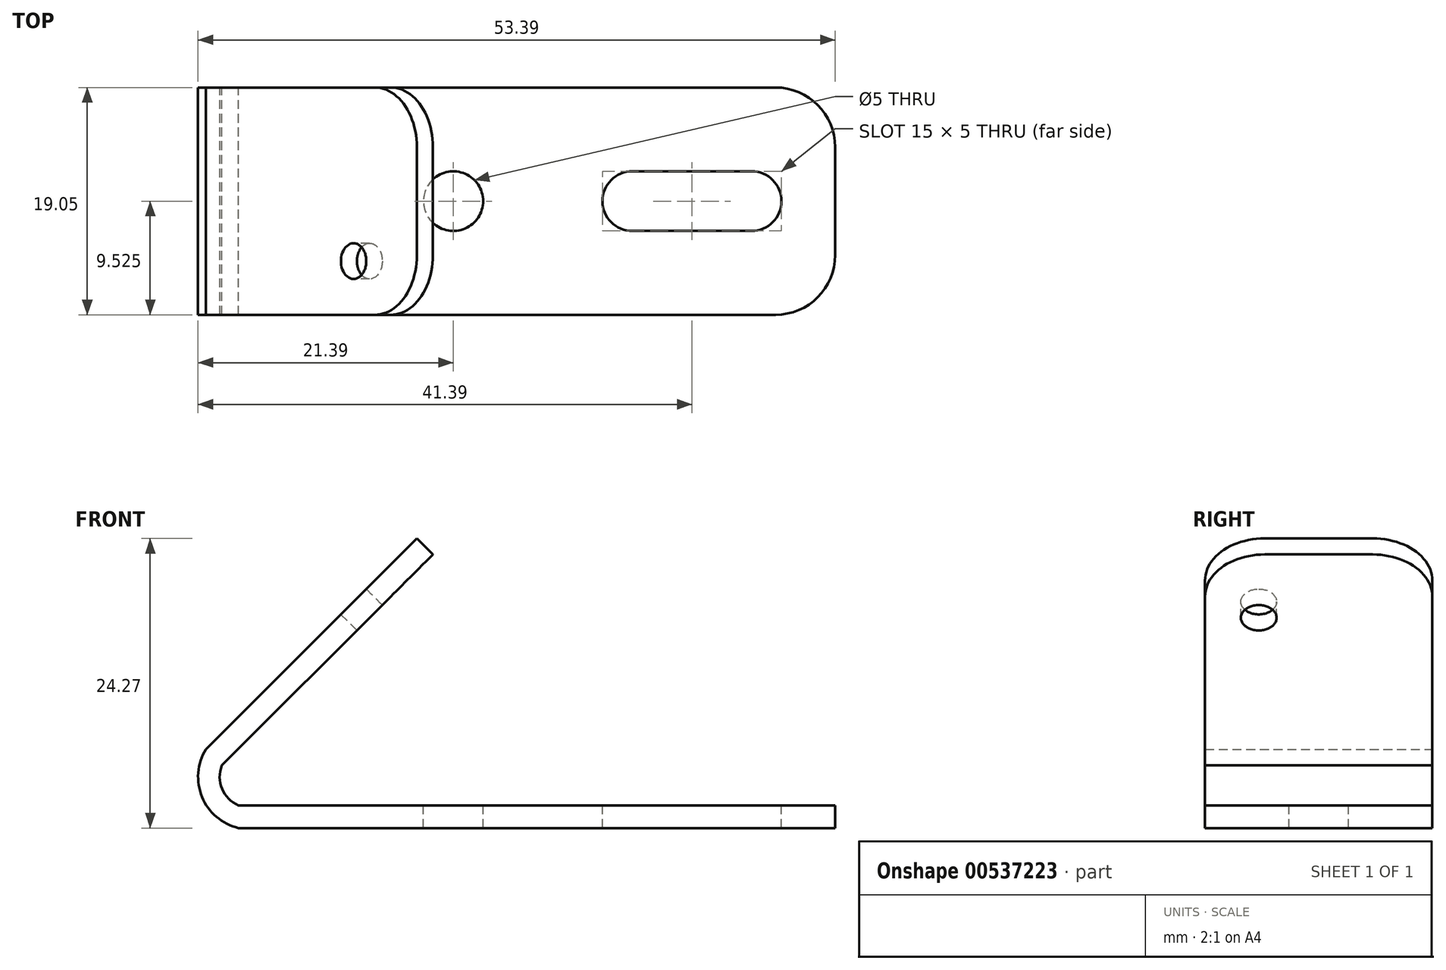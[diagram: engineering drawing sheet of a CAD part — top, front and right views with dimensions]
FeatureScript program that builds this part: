
annotation { "Feature Type Name" : "Feature", "Feature Type Description" : "" }
export const myFeature = defineFeature(function(context is Context, id is Id, definition is map)
    precondition{}
    {
        {
            var Q0;
            Q0=qCreatedBy(makeId("Front.planeOp"),FACE);
            var sketch = newSketch(context, id + "F0", { "sketchPlane" : qUnion([Q0])});
            skLineSegment(sketch, "E0", {"start": v(0, 0) * mm, "end": v(50, 0) * mm});
            skLineSegment(sketch, "E1", {"start": v(50, 0) * mm, "end": v(50, 1.9) * mm});
            skLineSegment(sketch, "E2", {"start": v(50, 1.9) * mm, "end": v(0, 1.9) * mm});
            skLineSegment(sketch, "E3", {"start": v(-2.73, 6.6) * mm, "end": v(14.95, 24.27) * mm});
            skArc(sketch, "E4", {"start": v(-2.73, 6.6) * mm, "mid": v(-3.05, 2.6) * mm, "end": v(0, 0) * mm});
            skLineSegment(sketch, "E5", {"start": v(14.95, 24.27) * mm, "end": v(16.29, 22.93) * mm});
            skLineSegment(sketch, "E6", {"start": v(16.29, 22.93) * mm, "end": v(-1.39, 5.25) * mm});
            skArc(sketch, "E7", {"start": v(0, 1.9) * mm, "mid": v(-1.38, 3.3) * mm, "end": v(-1.39, 5.25) * mm});
            skSolve(sketch);
        }
        {
            var Q0;
            Q0 = qSketchRegion(id + "F0", true);
            extrude(context, id + "F1", {"entities" : qUnion([Q0]), "depth" : 19.05 * mm, "offsetDistance" : 25 * mm});
        }
        {
            var Q0;
            Q0=makeQuery(id+"F1.opExtrude","CAP_EDGE",EDGE,{"disambiguationData":[OSD([sQuery(id+"F0.wireOp",EDGE,"E5")])],"isStart":false});
            var Q1;
            Q1=makeQuery(id+"F1.opExtrude","CAP_EDGE",EDGE,{"disambiguationData":[OSD([sQuery(id+"F0.wireOp",EDGE,"E5")])],"isStart":true});
            fillet(context, id + "F2", {"entities" : qUnion([Q0, Q1]), "radius" : 5 * mm, "tangentPropagation" : true, "allowEdgeOverflow" : false});
        }
        {
            var Q0;
            Q0=makeQuery(id+"F1.opExtrude","SWEPT_FACE",FACE,{"disambiguationData":[OSD([sQuery(id+"F0.wireOp",EDGE,"E3")])]});
            var sketch = newSketch(context, id + "F3", { "sketchPlane" : qUnion([Q0])});
            skLineSegment(sketch, "E8", {"start": v(19.05, 27.73) * mm, "end": v(14.55, 27.73) * mm, "construction": true});
            skLineSegment(sketch, "E9", {"start": v(14.55, 27.73) * mm, "end": v(14.55, 20.23) * mm, "construction": true});
            skCircle(sketch, "E10", {"center": v(14.55, 20.23) * mm, "radius": 1.5 * mm});
            skLineSegment(sketch, "E11", {"start": v(9.53, 42.7) * mm, "end": v(9.53, -11.02) * mm, "construction": true});
            skPoint(sketch, "E11.startSnap0", {"position": v(9.53, 27.73) * mm});
            skCircle(sketch, "E12.MirrorC", {"center": v(4.5, 20.23) * mm, "radius": 1.5 * mm});
            skSolve(sketch);
        }
        {
            var Q0;
            Q0=makeQuery(id+"F3.imprint","IMPRINT",FACE,{"disambiguationData":[TD([[makeQuery(id+"F3.imprint","IMPRINT",EDGE,{"derivedFrom":sQuery(id+"F3.wireOp",EDGE,"E10")}),1.0]])]});
            extrude(context, id + "F4", {"entities" : qUnion([Q0]), "operationType" : NewBodyOperationType.REMOVE, "oppositeDirection" : true, "depth" : 10 * mm, "offsetDistance" : 25 * mm});
        }
        {
            var Q0;
            Q0=makeQuery(id+"F1.opExtrude","CAP_EDGE",EDGE,{"disambiguationData":[OSD([sQuery(id+"F0.wireOp",EDGE,"E3")])],"isStart":true});
            cPoint(context, id + "F5", {"entities" : qUnion([Q0]), "parameter" : 0.5});
        }
        {
            var Q0;
            Q0=makeQuery(id+"F1.opExtrude","CAP_EDGE",EDGE,{"disambiguationData":[OSD([sQuery(id+"F0.wireOp",EDGE,"E3")])],"isStart":false});
            cPoint(context, id + "F6", {"entities" : qUnion([Q0]), "parameter" : 0.5});
        }
        {
            var Q0;
            Q0 = qCreatedBy(id + "F5" ,VERTEX);
            var Q1;
            Q1 = qCreatedBy(id + "F6" ,VERTEX);
            cPlane(context, id + "F7", {"entities" : qUnion([Q0, Q1]), "cplaneType" : CPlaneType.MID_PLANE, "offset" : 25 * mm, "width" : 150 * mm, "height" : 150 * mm});
        }
        {
            var Q0;
            Q0=makeQuery(id+"F1.opExtrude","CAP_EDGE",EDGE,{"disambiguationData":[OSD([sQuery(id+"F0.wireOp",EDGE,"E1")])],"isStart":true});
            var Q1;
            Q1=makeQuery(id+"F1.opExtrude","CAP_EDGE",EDGE,{"disambiguationData":[OSD([sQuery(id+"F0.wireOp",EDGE,"E1")])],"isStart":false});
            fillet(context, id + "F8", {"entities" : qUnion([Q0, Q1]), "radius" : 5 * mm, "tangentPropagation" : true, "allowEdgeOverflow" : false});
        }
        {
            var Q0;
            Q0=makeQuery(id+"F1.opExtrude","SWEPT_FACE",FACE,{"disambiguationData":[OSD([sQuery(id+"F0.wireOp",EDGE,"E2")])]});
            var sketch = newSketch(context, id + "F9", { "sketchPlane" : qUnion([Q0])});
            skArc(sketch, "E13", {"start": v(43, -12.03) * mm, "mid": v(45.5, -9.53) * mm, "end": v(43, -7.03) * mm});
            skPoint(sketch, "E13.centerSnap0", {"position": v(50, -9.53) * mm});
            skArc(sketch, "E14", {"start": v(33, -7.03) * mm, "mid": v(30.5, -9.53) * mm, "end": v(33, -12.03) * mm});
            skLineSegment(sketch, "E15", {"start": v(33, -7.03) * mm, "end": v(43, -7.03) * mm});
            skLineSegment(sketch, "E16", {"start": v(33, -12.03) * mm, "end": v(43, -12.03) * mm});
            skCircle(sketch, "E17", {"center": v(18, -9.53) * mm, "radius": 2.5 * mm});
            skSolve(sketch);
        }
        {
            var Q0;
            Q0=makeQuery(id+"F9.imprint","IMPRINT",FACE,{"disambiguationData":[TD([[makeQuery(id+"F9.imprint","IMPRINT",EDGE,{"derivedFrom":sQuery(id+"F9.wireOp",EDGE,"E17")}),1.0]])]});
            var Q1;
            Q1=makeQuery(id+"F9.imprint","IMPRINT",FACE,{"disambiguationData":[TD([[makeQuery(id+"F9.imprint","IMPRINT",EDGE,{"derivedFrom":sQuery(id+"F9.wireOp",EDGE,"E13")}),1.0]])]});
            extrude(context, id + "F10", {"entities" : qUnion([Q0, Q1]), "operationType" : NewBodyOperationType.REMOVE, "oppositeDirection" : true, "depth" : 25 * mm, "offsetDistance" : 25 * mm});
        }
    });
